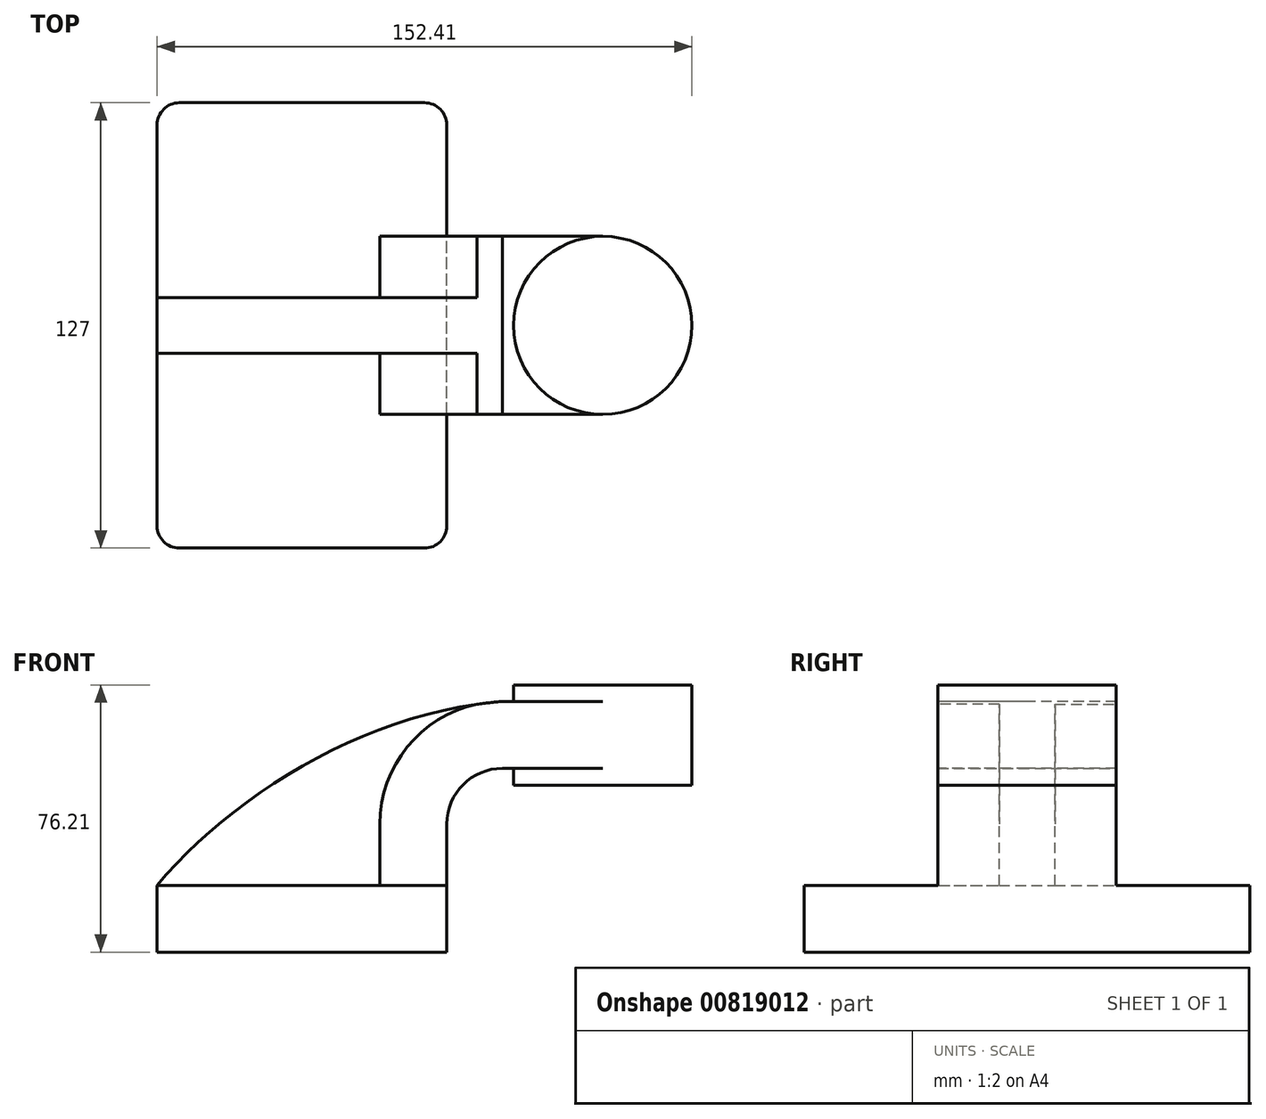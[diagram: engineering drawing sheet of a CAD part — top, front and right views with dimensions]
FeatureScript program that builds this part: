
annotation { "Feature Type Name" : "Feature", "Feature Type Description" : "" }
export const myFeature = defineFeature(function(context is Context, id is Id, definition is map)
    precondition{}
    {
        {
            var Q0;
            Q0=qCreatedBy(makeId("Front.planeOp"),FACE);
            var sketch = newSketch(context, id + "F0", { "sketchPlane" : qUnion([Q0])});
            skLineSegment(sketch, "E0.bottom", {"start": v(-41.28, -9.53) * mm, "end": v(41.28, -9.53) * mm});
            skLineSegment(sketch, "E0.top", {"start": v(-41.28, 9.52) * mm, "end": v(41.28, 9.52) * mm});
            skLineSegment(sketch, "E0.left", {"start": v(-41.27, -9.53) * mm, "end": v(-41.28, 9.52) * mm});
            skLineSegment(sketch, "E0.right", {"start": v(41.28, -9.53) * mm, "end": v(41.28, 9.52) * mm});
            skPoint(sketch, "E0.middle", {"position": v(0, 0) * mm});
            skLineSegment(sketch, "E1.bottom", {"start": v(60.32, 38.1) * mm, "end": v(111.12, 38.1) * mm});
            skLineSegment(sketch, "E1.top", {"start": v(60.32, 66.67) * mm, "end": v(111.12, 66.67) * mm});
            skLineSegment(sketch, "E1.left", {"start": v(60.32, 38.1) * mm, "end": v(60.32, 66.67) * mm});
            skLineSegment(sketch, "E1.right", {"start": v(111.12, 38.1) * mm, "end": v(111.12, 66.67) * mm});
            skPoint(sketch, "E1.middle", {"position": v(85.72, 52.39) * mm});
            skLineSegment(sketch, "E2", {"start": v(41.27, 9.52) * mm, "end": v(41.27, 27) * mm});
            skArc(sketch, "E3", {"start": v(41.27, 27) * mm, "mid": v(45.92, 38.23) * mm, "end": v(57.15, 42.88) * mm});
            skLineSegment(sketch, "E4", {"start": v(57.15, 42.88) * mm, "end": v(85.72, 42.88) * mm});
            skLineSegment(sketch, "E5.0", {"start": v(57.15, 61.93) * mm, "end": v(85.72, 61.93) * mm});
            skArc(sketch, "E5.1", {"start": v(22.22, 27) * mm, "mid": v(32.45, 51.7) * mm, "end": v(57.15, 61.93) * mm});
            skLineSegment(sketch, "E5.2", {"start": v(22.22, 9.52) * mm, "end": v(22.22, 27) * mm});
            skLineSegment(sketch, "E6", {"start": v(85.72, 38.1) * mm, "end": v(85.72, 66.67) * mm});
            skPoint(sketch, "E7", {"position": v(85.72, 38.1) * mm});
            skFitSpline(sketch, "E8", {"points": [v(-41.28, 9.53) * mm, v(57.15, 61.93) * mm], "startDerivative": vector(63.87, 76.05) * mm, "endDerivative": vector(117.57, 8.5) * mm});
            skSolve(sketch);
        }
        {
            var Q0;
            Q0=makeQuery(id+"F0.imprint","IMPRINT",FACE,{"disambiguationData":[TD([[makeQuery(id+"F0.imprint","IMPRINT",EDGE,{"derivedFrom":sQuery(id+"F0.wireOp",EDGE,"E0.bottom")}),1.0]])]});
            extrude(context, id + "F1", {"entities" : qUnion([Q0]), "endBound" : BoundingType.SYMMETRIC, "depth" : 127 * mm, "offsetDistance" : 25.4 * mm});
        }
        {
            var Q0;
            {var subQ0=sQuery(id+"F0.wireOp",EDGE,"E4");var subQ1=sQuery(id+"F0.wireOp",EDGE,"E1.left");var subQ2=makeQuery(id+"F0.imprint","INTERSECT",VERTEX,{"derivedFrom":[subQ1,subQ0]});Q0=makeQuery(id+"F0.imprint","IMPRINT",FACE,{"disambiguationData":[TD([[makeQuery(id+"F0.imprint","IMPRINT",EDGE,{"disambiguationData":[TD([[subQ2,-1.0]])],"derivedFrom":subQ1}),-1.0]])]});}
            var Q1;
            {var subQ1=sQuery(id+"F0.wireOp",EDGE,"E2");Q1=makeQuery(id+"F0.imprint","IMPRINT",FACE,{"disambiguationData":[TD([[makeQuery(id+"F0.imprint","IMPRINT",EDGE,{"derivedFrom":subQ1}),1.0]])]});}
            extrude(context, id + "F2", {"entities" : qUnion([Q0, Q1]), "operationType" : NewBodyOperationType.ADD, "endBound" : BoundingType.SYMMETRIC, "depth" : 50.8 * mm, "offsetDistance" : 25.4 * mm});
        }
        {
            var Q0;
            {var subQ3=sQuery(id+"F0.wireOp",EDGE,"E5.2");Q0=makeQuery(id+"F0.imprint","IMPRINT",FACE,{"disambiguationData":[TD([[makeQuery(id+"F0.imprint","IMPRINT",EDGE,{"derivedFrom":subQ3}),1.0]])]});}
            extrude(context, id + "F3", {"entities" : qUnion([Q0]), "operationType" : NewBodyOperationType.ADD, "endBound" : BoundingType.SYMMETRIC, "depth" : 15.88 * mm, "offsetDistance" : 25.4 * mm});
        }
        {
            var Q0;
            {var subQ4=sQuery(id+"F0.wireOp",EDGE,"E1.right");Q0=makeQuery(id+"F0.imprint","IMPRINT",FACE,{"disambiguationData":[TD([[makeQuery(id+"F0.imprint","IMPRINT",EDGE,{"derivedFrom":subQ4}),1.0]])]});}
            var Q1;
            Q1=sQuery(id+"F0.wireOp",EDGE,"E6");
            revolve(context, id + "F4", {"operationType" : NewBodyOperationType.ADD, "surfaceOperationType" : NewSurfaceOperationType.NEW, "entities" : qUnion([Q0]), "axis" : qUnion([Q1]), "revolveType" : RevolveType.FULL});
        }
        {
            var Q0;
            Q0=makeQuery(id+"F1.opExtrude","CAP_EDGE",EDGE,{"disambiguationData":[OSD([sQuery(id+"F0.wireOp",EDGE,"E0.right")])],"isStart":false});
            var Q1;
            Q1=makeQuery(id+"F1.opExtrude","CAP_EDGE",EDGE,{"disambiguationData":[OSD([sQuery(id+"F0.wireOp",EDGE,"E0.left")])],"isStart":false});
            var Q2;
            Q2=makeQuery(id+"F1.opExtrude","CAP_EDGE",EDGE,{"disambiguationData":[OSD([sQuery(id+"F0.wireOp",EDGE,"E0.right")])],"isStart":true});
            var Q3;
            Q3=makeQuery(id+"F1.opExtrude","CAP_EDGE",EDGE,{"disambiguationData":[OSD([sQuery(id+"F0.wireOp",EDGE,"E0.left")])],"isStart":true});
            fillet(context, id + "F5", {"entities" : qUnion([Q0, Q1, Q2, Q3]), "radius" : 6.35 * mm, "tangentPropagation" : true, "allowEdgeOverflow" : false});
        }
    });
